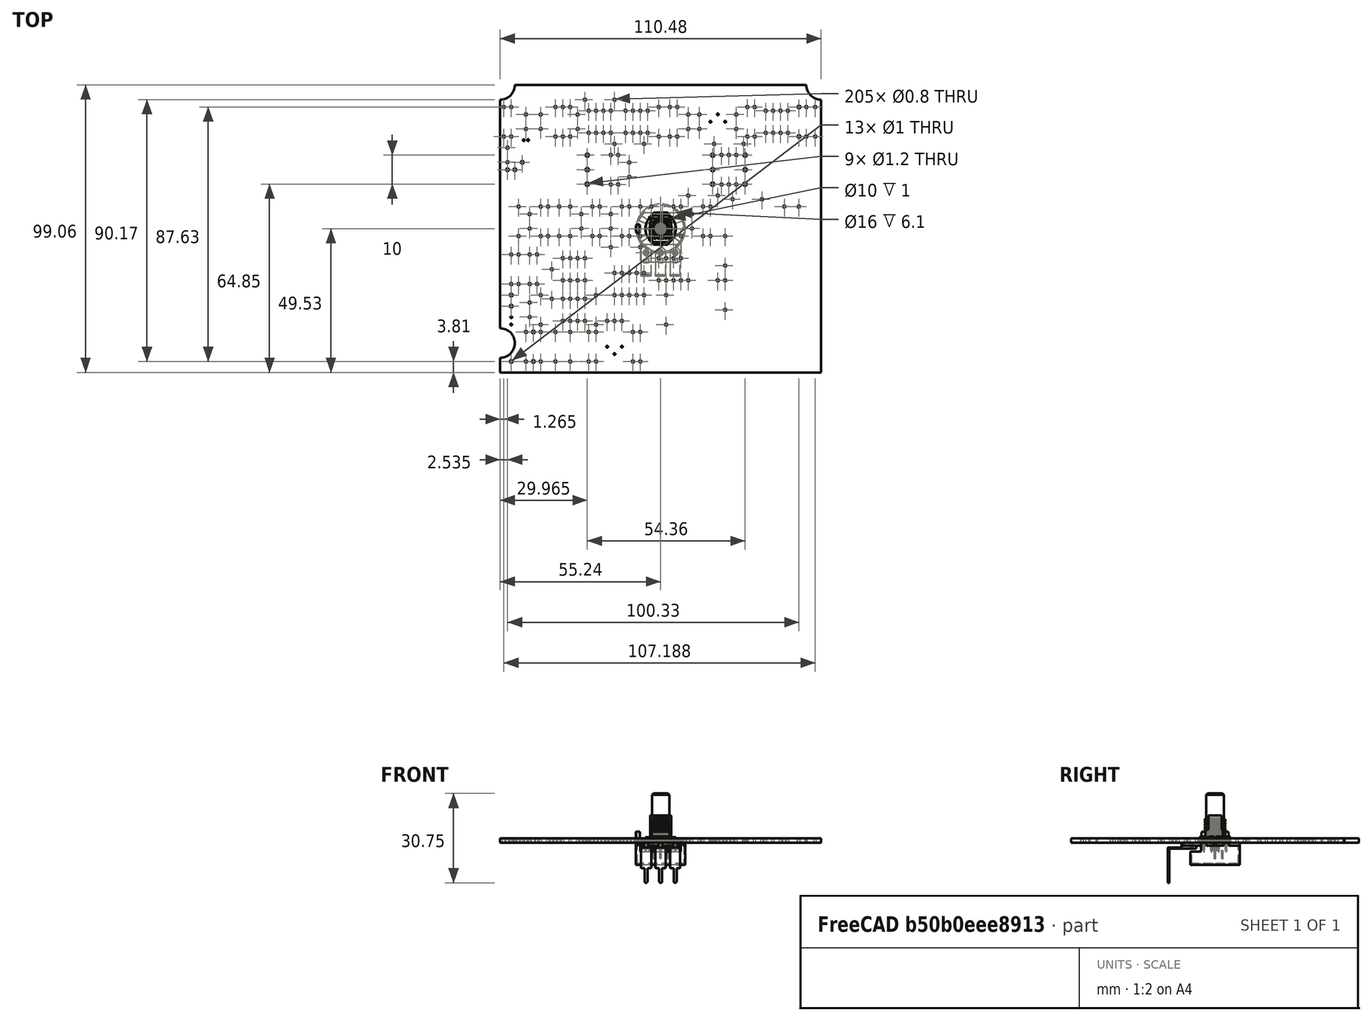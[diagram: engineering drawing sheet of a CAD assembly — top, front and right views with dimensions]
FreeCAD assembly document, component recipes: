
FREECAD ASSEMBLY — COMPONENT RECIPES ("PRJ-003-#000-000 - Lid Assy")

This assembly document has 56 components, labeled P0..P55 below (a component is one placed body or linked part). 0 of them carry a construction recipe — the FreeCAD feature program that regenerates the part from scratch, quoted from this document or its linked companion documents; the rest are supplied as boundary geometry only. No exploded tour is included for this assembly.
COMPONENT P0 — geometry summary ("R_CC25_P10.16_H_27k001"; no construction recipe available for this part):
  bounding box: 10.7 x 5.1 x 2.5 mm
  tessellated surface: 9,712 triangles
  volume: 35 mm^3 (25% of its bounding box)
  symmetry: 2-fold rotationally symmetric about the z axis; mirror-symmetric across its x mid-plane, y mid-plane
COMPONENT P1 — geometry summary ("R_CC25_P10.16_H_47k001"; no construction recipe available for this part):
  bounding box: 10.7 x 5.1 x 2.5 mm
  tessellated surface: 9,712 triangles
  volume: 35 mm^3 (25% of its bounding box)
  symmetry: 2-fold rotationally symmetric about the z axis; mirror-symmetric across its x mid-plane, y mid-plane
COMPONENT P2 — geometry summary ("R_CC25_P10.16_H_560R001"; no construction recipe available for this part):
  bounding box: 10.7 x 5.1 x 2.5 mm
  tessellated surface: 9,712 triangles
  volume: 35 mm^3 (25% of its bounding box)
  symmetry: 2-fold rotationally symmetric about the z axis; mirror-symmetric across its x mid-plane, y mid-plane
COMPONENT P3 — geometry summary ("R_CC25_P10.16_H_27k002"; no construction recipe available for this part):
  bounding box: 10.7 x 5.1 x 2.5 mm
  tessellated surface: 9,712 triangles
  volume: 35 mm^3 (25% of its bounding box)
  symmetry: 2-fold rotationally symmetric about the z axis; mirror-symmetric across its x mid-plane, y mid-plane
COMPONENT P4 — geometry summary ("R_CC25_P10.16_H_10k001"; no construction recipe available for this part):
  bounding box: 10.7 x 5.1 x 2.5 mm
  tessellated surface: 9,712 triangles
  volume: 35 mm^3 (25% of its bounding box)
  symmetry: 2-fold rotationally symmetric about the z axis; mirror-symmetric across its x mid-plane, y mid-plane
COMPONENT P5 — geometry summary ("R_CC25_P10.16_H_8.2k001"; no construction recipe available for this part):
  bounding box: 10.7 x 5.1 x 2.5 mm
  tessellated surface: 9,712 triangles
  volume: 35 mm^3 (25% of its bounding box)
  symmetry: 2-fold rotationally symmetric about the z axis; mirror-symmetric across its x mid-plane, y mid-plane
COMPONENT P6 — geometry summary ("R_CC25_P10.16_H_10k002"; no construction recipe available for this part):
  bounding box: 10.7 x 5.1 x 2.5 mm
  tessellated surface: 9,712 triangles
  volume: 35 mm^3 (25% of its bounding box)
  symmetry: 2-fold rotationally symmetric about the z axis; mirror-symmetric across its x mid-plane, y mid-plane
COMPONENT P7 — geometry summary ("R_CC25_P10.16_H_220k001"; no construction recipe available for this part):
  bounding box: 10.7 x 5.1 x 2.5 mm
  tessellated surface: 9,712 triangles
  volume: 35 mm^3 (25% of its bounding box)
  symmetry: 2-fold rotationally symmetric about the z axis; mirror-symmetric across its x mid-plane, y mid-plane
COMPONENT P8 — geometry summary ("R_CC25_P10.16_H_4.7k001"; no construction recipe available for this part):
  bounding box: 10.7 x 5.1 x 2.5 mm
  tessellated surface: 9,712 triangles
  volume: 35 mm^3 (25% of its bounding box)
  symmetry: 2-fold rotationally symmetric about the z axis; mirror-symmetric across its x mid-plane, y mid-plane
COMPONENT P9 — geometry summary ("R_CC25_P10.16_H_220k002"; no construction recipe available for this part):
  bounding box: 10.7 x 5.1 x 2.5 mm
  tessellated surface: 9,712 triangles
  volume: 35 mm^3 (25% of its bounding box)
  symmetry: 2-fold rotationally symmetric about the z axis; mirror-symmetric across its x mid-plane, y mid-plane
COMPONENT P10 — geometry summary ("R_CC25_P10.16_H_4.7k002"; no construction recipe available for this part):
  bounding box: 10.7 x 5.1 x 2.5 mm
  tessellated surface: 9,712 triangles
  volume: 35 mm^3 (25% of its bounding box)
  symmetry: 2-fold rotationally symmetric about the z axis; mirror-symmetric across its x mid-plane, y mid-plane
COMPONENT P11 — geometry summary ("R_CC25_P10.16_H_4.7k003"; no construction recipe available for this part):
  bounding box: 10.7 x 5.1 x 2.5 mm
  tessellated surface: 9,712 triangles
  volume: 35 mm^3 (25% of its bounding box)
  symmetry: 2-fold rotationally symmetric about the z axis; mirror-symmetric across its x mid-plane, y mid-plane
COMPONENT P12 — geometry summary ("R_CC25_P10.16_H_220k003"; no construction recipe available for this part):
  bounding box: 10.7 x 5.1 x 2.5 mm
  tessellated surface: 9,712 triangles
  volume: 35 mm^3 (25% of its bounding box)
  symmetry: 2-fold rotationally symmetric about the z axis; mirror-symmetric across its x mid-plane, y mid-plane
COMPONENT P13 — geometry summary ("R_CC25_P10.16_H_4.7k004"; no construction recipe available for this part):
  bounding box: 10.7 x 5.1 x 2.5 mm
  tessellated surface: 9,712 triangles
  volume: 35 mm^3 (25% of its bounding box)
  symmetry: 2-fold rotationally symmetric about the z axis; mirror-symmetric across its x mid-plane, y mid-plane
COMPONENT P14 — geometry summary ("R_CC25_P10.16_H_4.7k005"; no construction recipe available for this part):
  bounding box: 10.7 x 5.1 x 2.5 mm
  tessellated surface: 9,712 triangles
  volume: 35 mm^3 (25% of its bounding box)
  symmetry: 2-fold rotationally symmetric about the z axis; mirror-symmetric across its x mid-plane, y mid-plane
COMPONENT P15 — geometry summary ("R_CC25_P10.16_H_220k004"; no construction recipe available for this part):
  bounding box: 10.7 x 5.1 x 2.5 mm
  tessellated surface: 9,712 triangles
  volume: 35 mm^3 (25% of its bounding box)
  symmetry: 2-fold rotationally symmetric about the z axis; mirror-symmetric across its x mid-plane, y mid-plane
COMPONENT P16 — geometry summary ("R_CC25_P10.16_H_4.7k006"; no construction recipe available for this part):
  bounding box: 10.7 x 5.1 x 2.5 mm
  tessellated surface: 9,712 triangles
  volume: 35 mm^3 (25% of its bounding box)
  symmetry: 2-fold rotationally symmetric about the z axis; mirror-symmetric across its x mid-plane, y mid-plane
COMPONENT P17 — geometry summary ("R_CC25_P10.16_H_4.7k007"; no construction recipe available for this part):
  bounding box: 10.7 x 5.1 x 2.5 mm
  tessellated surface: 9,712 triangles
  volume: 35 mm^3 (25% of its bounding box)
  symmetry: 2-fold rotationally symmetric about the z axis; mirror-symmetric across its x mid-plane, y mid-plane
COMPONENT P18 — geometry summary ("R_CC25_P10.16_H_220k005"; no construction recipe available for this part):
  bounding box: 10.7 x 5.1 x 2.5 mm
  tessellated surface: 9,712 triangles
  volume: 35 mm^3 (25% of its bounding box)
  symmetry: 2-fold rotationally symmetric about the z axis; mirror-symmetric across its x mid-plane, y mid-plane
COMPONENT P19 — geometry summary ("R_CC25_P10.16_H_4.7k008"; no construction recipe available for this part):
  bounding box: 10.7 x 5.1 x 2.5 mm
  tessellated surface: 9,712 triangles
  volume: 35 mm^3 (25% of its bounding box)
  symmetry: 2-fold rotationally symmetric about the z axis; mirror-symmetric across its x mid-plane, y mid-plane
COMPONENT P20 — geometry summary ("R_CC25_P10.16_H_4.7k009"; no construction recipe available for this part):
  bounding box: 10.7 x 5.1 x 2.5 mm
  tessellated surface: 9,712 triangles
  volume: 35 mm^3 (25% of its bounding box)
  symmetry: 2-fold rotationally symmetric about the z axis; mirror-symmetric across its x mid-plane, y mid-plane
COMPONENT P21 — geometry summary ("R_CC25_P10.16_H_220k006"; no construction recipe available for this part):
  bounding box: 10.7 x 5.1 x 2.5 mm
  tessellated surface: 9,712 triangles
  volume: 35 mm^3 (25% of its bounding box)
  symmetry: 2-fold rotationally symmetric about the z axis; mirror-symmetric across its x mid-plane, y mid-plane
COMPONENT P22 — geometry summary ("R_CC25_P10.16_H_4.7k010"; no construction recipe available for this part):
  bounding box: 10.7 x 5.1 x 2.5 mm
  tessellated surface: 9,712 triangles
  volume: 35 mm^3 (25% of its bounding box)
  symmetry: 2-fold rotationally symmetric about the z axis; mirror-symmetric across its x mid-plane, y mid-plane
COMPONENT P23 — geometry summary ("R_CC25_P10.16_H_4.7k011"; no construction recipe available for this part):
  bounding box: 10.7 x 5.1 x 2.5 mm
  tessellated surface: 9,712 triangles
  volume: 35 mm^3 (25% of its bounding box)
  symmetry: 2-fold rotationally symmetric about the z axis; mirror-symmetric across its x mid-plane, y mid-plane
COMPONENT P24 — geometry summary ("R_CC25_P10.16_H_8.2k002"; no construction recipe available for this part):
  bounding box: 10.7 x 5.1 x 2.5 mm
  tessellated surface: 9,712 triangles
  volume: 35 mm^3 (25% of its bounding box)
  symmetry: 2-fold rotationally symmetric about the z axis; mirror-symmetric across its x mid-plane, y mid-plane
COMPONENT P25 — geometry summary ("R_CC25_P10.16_H_4.7k012"; no construction recipe available for this part):
  bounding box: 10.7 x 5.1 x 2.5 mm
  tessellated surface: 9,712 triangles
  volume: 35 mm^3 (25% of its bounding box)
  symmetry: 2-fold rotationally symmetric about the z axis; mirror-symmetric across its x mid-plane, y mid-plane
COMPONENT P26 — geometry summary ("R_CC25_P10.16_H_4.7k013"; no construction recipe available for this part):
  bounding box: 10.7 x 5.1 x 2.5 mm
  tessellated surface: 9,712 triangles
  volume: 35 mm^3 (25% of its bounding box)
  symmetry: 2-fold rotationally symmetric about the z axis; mirror-symmetric across its x mid-plane, y mid-plane
COMPONENT P27 — geometry summary ("R_CC25_P10.16_H_4.7k014"; no construction recipe available for this part):
  bounding box: 10.7 x 5.1 x 2.5 mm
  tessellated surface: 9,712 triangles
  volume: 35 mm^3 (25% of its bounding box)
  symmetry: 2-fold rotationally symmetric about the z axis; mirror-symmetric across its x mid-plane, y mid-plane
COMPONENT P28 — geometry summary ("R_CC25_P10.16_H_390k001"; no construction recipe available for this part):
  bounding box: 10.7 x 5.1 x 2.5 mm
  tessellated surface: 9,712 triangles
  volume: 35 mm^3 (25% of its bounding box)
  symmetry: 2-fold rotationally symmetric about the z axis; mirror-symmetric across its x mid-plane, y mid-plane
COMPONENT P29 — geometry summary ("Bourns_3362P-1-105"; no construction recipe available for this part):
  bounding box: 10.2 x 7.0 x 6.7 mm
  tessellated surface: 4,452 triangles
  volume: 191 mm^3 (40% of its bounding box)
COMPONENT P30 — geometry summary ("R_CF25_P10.16_H001"; no construction recipe available for this part):
  bounding box: 10.7 x 5.1 x 2.5 mm
  tessellated surface: 5,680 triangles
  volume: 34 mm^3 (25% of its bounding box)
  symmetry: 2-fold rotationally symmetric about the z axis; mirror-symmetric across its x mid-plane, y mid-plane
COMPONENT P31 — geometry summary ("R_CF25_P10.16_H002"; no construction recipe available for this part):
  bounding box: 10.7 x 5.1 x 2.5 mm
  tessellated surface: 5,680 triangles
  volume: 34 mm^3 (25% of its bounding box)
  symmetry: 2-fold rotationally symmetric about the z axis; mirror-symmetric across its x mid-plane, y mid-plane
COMPONENT P32 — geometry summary ("R_CF25_P10.16_H003"; no construction recipe available for this part):
  bounding box: 10.7 x 5.1 x 2.5 mm
  tessellated surface: 5,680 triangles
  volume: 34 mm^3 (25% of its bounding box)
  symmetry: 2-fold rotationally symmetric about the z axis; mirror-symmetric across its x mid-plane, y mid-plane
COMPONENT P33 — geometry summary ("R_CF25_P10.16_H004"; no construction recipe available for this part):
  bounding box: 10.7 x 5.1 x 2.5 mm
  tessellated surface: 5,680 triangles
  volume: 34 mm^3 (25% of its bounding box)
  symmetry: 2-fold rotationally symmetric about the z axis; mirror-symmetric across its x mid-plane, y mid-plane
COMPONENT P34 — geometry summary ("R_CF25_P10.16_H005"; no construction recipe available for this part):
  bounding box: 10.7 x 5.1 x 2.5 mm
  tessellated surface: 5,680 triangles
  volume: 34 mm^3 (25% of its bounding box)
  symmetry: 2-fold rotationally symmetric about the z axis; mirror-symmetric across its x mid-plane, y mid-plane
COMPONENT P35 — geometry summary ("R_CF25_P10.16_H006"; no construction recipe available for this part):
  bounding box: 10.7 x 5.1 x 2.5 mm
  tessellated surface: 5,680 triangles
  volume: 34 mm^3 (25% of its bounding box)
  symmetry: 2-fold rotationally symmetric about the z axis; mirror-symmetric across its x mid-plane, y mid-plane
COMPONENT P36 — geometry summary ("R_CF25_P10.16_H007"; no construction recipe available for this part):
  bounding box: 10.7 x 5.1 x 2.5 mm
  tessellated surface: 5,680 triangles
  volume: 34 mm^3 (25% of its bounding box)
  symmetry: 2-fold rotationally symmetric about the z axis; mirror-symmetric across its x mid-plane, y mid-plane
COMPONENT P37 — geometry summary ("R_CF25_P10.16_H008"; no construction recipe available for this part):
  bounding box: 10.7 x 5.1 x 2.5 mm
  tessellated surface: 5,680 triangles
  volume: 34 mm^3 (25% of its bounding box)
  symmetry: 2-fold rotationally symmetric about the z axis; mirror-symmetric across its x mid-plane, y mid-plane
COMPONENT P38 — geometry summary ("R_CF25_P10.16_H009"; no construction recipe available for this part):
  bounding box: 10.7 x 5.1 x 2.5 mm
  tessellated surface: 5,680 triangles
  volume: 34 mm^3 (25% of its bounding box)
  symmetry: 2-fold rotationally symmetric about the z axis; mirror-symmetric across its x mid-plane, y mid-plane
COMPONENT P39 — geometry summary ("R_CF25_P10.16_H010"; no construction recipe available for this part):
  bounding box: 10.7 x 5.1 x 2.5 mm
  tessellated surface: 5,680 triangles
  volume: 34 mm^3 (25% of its bounding box)
  symmetry: 2-fold rotationally symmetric about the z axis; mirror-symmetric across its x mid-plane, y mid-plane
COMPONENT P40 — geometry summary ("R_CF25_P10.16_H011"; no construction recipe available for this part):
  bounding box: 10.7 x 5.1 x 2.5 mm
  tessellated surface: 5,680 triangles
  volume: 34 mm^3 (25% of its bounding box)
  symmetry: 2-fold rotationally symmetric about the z axis; mirror-symmetric across its x mid-plane, y mid-plane
COMPONENT P41 — geometry summary ("Texas_Instruments_RC4558P001"; no construction recipe available for this part):
  bounding box: 9.6 x 7.9 x 7.1 mm
  tessellated surface: 2,606 triangles
  volume: 205 mm^3 (38% of its bounding box)
  symmetry: mirror-symmetric across its y mid-plane
COMPONENT P42 — geometry summary ("Texas_Instruments_RC4558P002"; no construction recipe available for this part):
  bounding box: 9.6 x 7.9 x 7.1 mm
  tessellated surface: 2,606 triangles
  volume: 205 mm^3 (38% of its bounding box)
  symmetry: mirror-symmetric across its y mid-plane
COMPONENT P43 — geometry summary ("Texas_Instruments_RC4558P003"; no construction recipe available for this part):
  bounding box: 9.6 x 7.9 x 7.1 mm
  tessellated surface: 2,606 triangles
  volume: 205 mm^3 (38% of its bounding box)
  symmetry: mirror-symmetric across its y mid-plane
COMPONENT P44 — geometry summary ("Texas_Instruments_RC4558P004"; no construction recipe available for this part):
  bounding box: 9.6 x 7.9 x 7.1 mm
  tessellated surface: 2,606 triangles
  volume: 205 mm^3 (38% of its bounding box)
  symmetry: mirror-symmetric across its y mid-plane
COMPONENT P45 — geometry summary ("Texas_Instruments_RC4558P005"; no construction recipe available for this part):
  bounding box: 9.6 x 7.9 x 7.1 mm
  tessellated surface: 2,606 triangles
  volume: 205 mm^3 (38% of its bounding box)
  symmetry: mirror-symmetric across its y mid-plane
COMPONENT P46 — geometry summary ("RV16AF-41-15R001"; no construction recipe available for this part):
  bounding box: 30.7 x 24.7 x 17.0 mm
  tessellated surface: 25,928 triangles
  volume: 1291 mm^3 (10% of its bounding box)
COMPONENT P47 — geometry summary ("RV16AF-41-15R002"; no construction recipe available for this part):
  bounding box: 30.7 x 24.7 x 17.0 mm
  tessellated surface: 25,928 triangles
  volume: 1291 mm^3 (10% of its bounding box)
COMPONENT P48 — geometry summary ("DO-35_P10.017"; no construction recipe available for this part):
  bounding box: 10.7 x 4.3 x 1.7 mm
  tessellated surface: 11,868 triangles
  volume: 11 mm^3 (14% of its bounding box)
  symmetry: 2-fold rotationally symmetric about the z axis; mirror-symmetric across its x mid-plane, y mid-plane
COMPONENT P49 — geometry summary ("Wima_MKS2C034701C00KSSD001"; no construction recipe available for this part):
  bounding box: 10.5 x 7.2 x 3.6 mm
  tessellated surface: 4,484 triangles
  volume: 188 mm^3 (70% of its bounding box)
  symmetry: 2-fold rotationally symmetric about the z axis; mirror-symmetric across its y mid-plane
COMPONENT P50 — geometry summary ("Wima_FKS2G016801B00KSSD001"; no construction recipe available for this part):
  bounding box: 9.5 x 7.2 x 3.1 mm
  tessellated surface: 4,784 triangles
  volume: 140 mm^3 (67% of its bounding box)
  symmetry: 2-fold rotationally symmetric about the z axis; mirror-symmetric across its y mid-plane
COMPONENT P51 — geometry summary ("Wima_FKS2G016801B00KSSD002"; no construction recipe available for this part):
  bounding box: 9.5 x 7.2 x 3.1 mm
  tessellated surface: 4,784 triangles
  volume: 140 mm^3 (67% of its bounding box)
  symmetry: 2-fold rotationally symmetric about the z axis; mirror-symmetric across its y mid-plane
COMPONENT P52 — geometry summary ("Wima_FKS2G016801B00KSSD003"; no construction recipe available for this part):
  bounding box: 9.5 x 7.2 x 3.1 mm
  tessellated surface: 4,784 triangles
  volume: 140 mm^3 (67% of its bounding box)
  symmetry: 2-fold rotationally symmetric about the z axis; mirror-symmetric across its y mid-plane
COMPONENT P53 — geometry summary ("Wima_FKS2G016801B00KSSD004"; no construction recipe available for this part):
  bounding box: 9.5 x 7.2 x 3.1 mm
  tessellated surface: 4,784 triangles
  volume: 140 mm^3 (67% of its bounding box)
  symmetry: 2-fold rotationally symmetric about the z axis; mirror-symmetric across its y mid-plane
COMPONENT P54 — geometry summary ("Wima_FKS2G016801B00KSSD005"; no construction recipe available for this part):
  bounding box: 9.5 x 7.2 x 3.1 mm
  tessellated surface: 4,784 triangles
  volume: 140 mm^3 (67% of its bounding box)
  symmetry: 2-fold rotationally symmetric about the z axis; mirror-symmetric across its y mid-plane
COMPONENT P55 — geometry summary ("Wima_FKS2G016801B00KSSD006"; no construction recipe available for this part):
  bounding box: 9.5 x 7.2 x 3.1 mm
  tessellated surface: 4,784 triangles
  volume: 140 mm^3 (67% of its bounding box)
  symmetry: 2-fold rotationally symmetric about the z axis; mirror-symmetric across its y mid-plane
PROVENANCE & LICENSES
A FreeCAD (.FCStd) document from a public repository crawl; recipes are the document's own serialized feature recipes (and, for linked parts, companion documents' recipes).
License: as declared in the source repository (recorded in the dataset sidecar).
